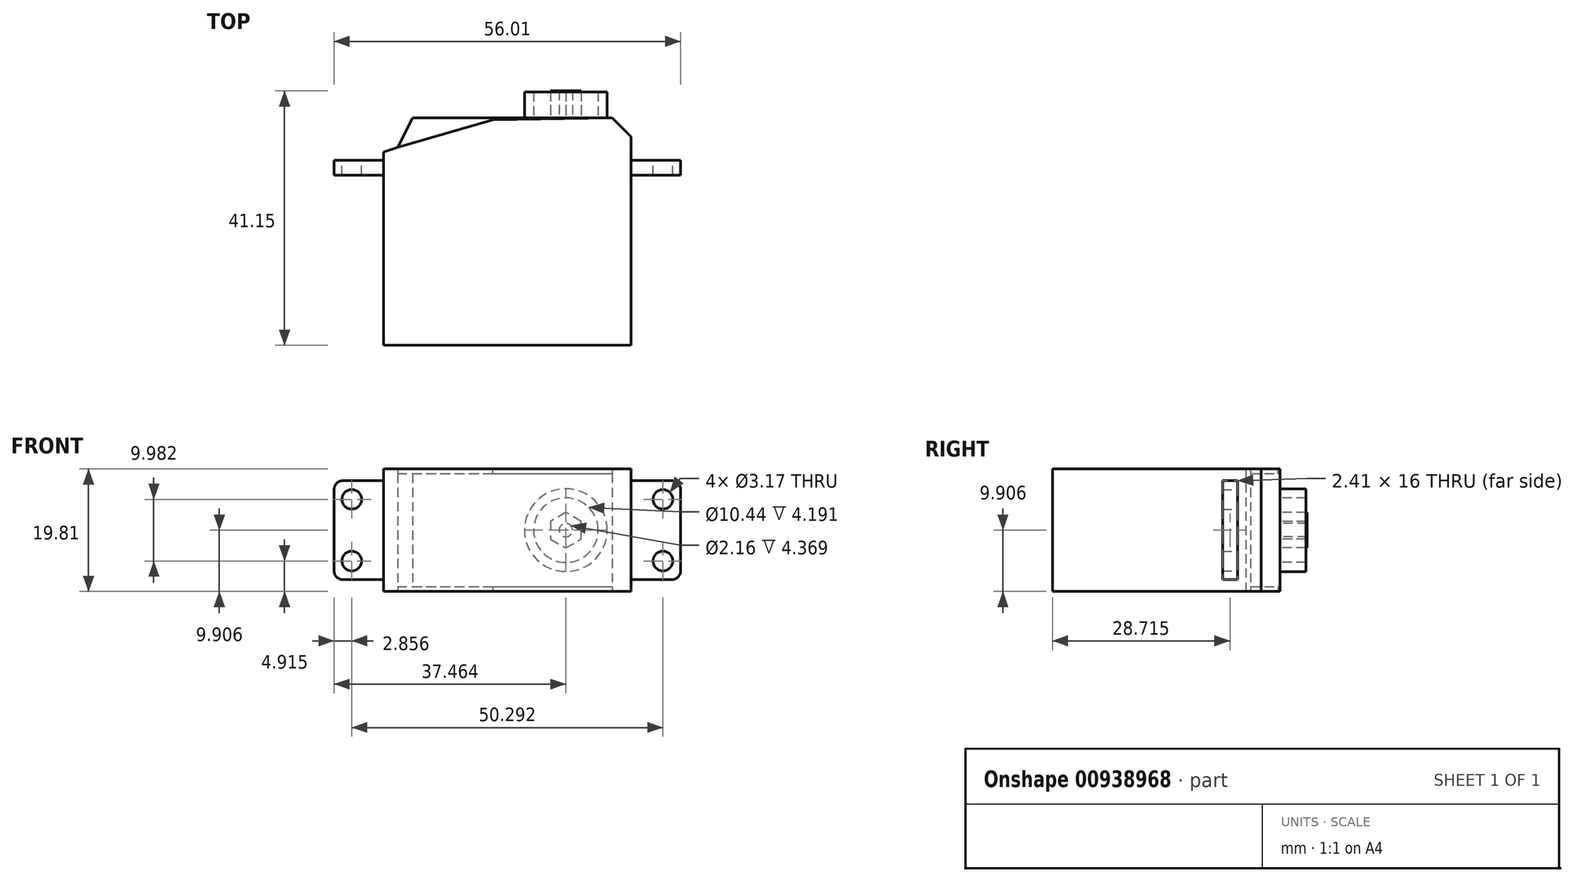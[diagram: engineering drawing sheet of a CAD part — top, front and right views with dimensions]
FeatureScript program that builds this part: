
annotation { "Feature Type Name" : "Feature", "Feature Type Description" : "" }
export const myFeature = defineFeature(function(context is Context, id is Id, definition is map)
    precondition{}
    {
        {
            var Q0;
            Q0=qCreatedBy(makeId("Top.planeOp"),FACE);
            var sketch = newSketch(context, id + "F0", { "sketchPlane" : qUnion([Q0])});
            skLineSegment(sketch, "E0.bottom", {"start": v(0, 0) * mm, "end": v(40, 0) * mm});
            skLineSegment(sketch, "E0.top", {"start": v(0, -36.78) * mm, "end": v(40, -36.78) * mm});
            skLineSegment(sketch, "E0.left", {"start": v(0, 0) * mm, "end": v(0, -36.78) * mm});
            skLineSegment(sketch, "E0.right", {"start": v(40, 0) * mm, "end": v(40, -36.78) * mm});
            skLineSegment(sketch, "E1", {"start": v(0, -5.54) * mm, "end": v(15.88, 0) * mm});
            skLineSegment(sketch, "E2", {"start": v(2.27, -4.75) * mm, "end": v(4.7, 0) * mm});
            skSolve(sketch);
        }
        {
            var Q0;
            {var subQ3=sQuery(id+"F0.wireOp",EDGE,"E0.top");Q0=makeQuery(id+"F0.imprint","IMPRINT",FACE,{"disambiguationData":[TD([[makeQuery(id+"F0.imprint","IMPRINT",EDGE,{"derivedFrom":subQ3}),1.0]])]});}
            extrude(context, id + "F1", {"entities" : qUnion([Q0]), "depth" : 19.8 * mm});
        }
        {
            var Q0;
            Q0=makeQuery(id+"F1.opExtrude","SWEPT_EDGE",EDGE,{"disambiguationData":[OSD([sQuery(id+"F0.wireOp",EDGE,"E0.bottom"),sQuery(id+"F0.wireOp",EDGE,"E0.right")])]});
            chamfer(context, id + "F2", {"entities" : qUnion([Q0]), "width" : 3.05 * mm, "tangentPropagation" : true});
        }
        {
            var Q0;
            {var subQ0=sQuery(id+"F0.wireOp",EDGE,"E2");Q0=makeQuery(id+"F0.imprint","IMPRINT",FACE,{"disambiguationData":[TD([[makeQuery(id+"F0.imprint","IMPRINT",EDGE,{"derivedFrom":subQ0}),-1.0]])]});}
            extrude(context, id + "F3", {"entities" : qUnion([Q0]), "operationType" : NewBodyOperationType.ADD, "depth" : 19.8 * mm});
        }
        {
            var Q0;
            Q0=makeQuery(id+"F1.opExtrude","SWEPT_FACE",FACE,{"disambiguationData":[OSD([sQuery(id+"F0.wireOp",EDGE,"E0.right")])]});
            var sketch = newSketch(context, id + "F4", { "sketchPlane" : qUnion([Q0])});
            skLineSegment(sketch, "E3.bottom", {"start": v(-6.86, 17.9) * mm, "end": v(-9.27, 17.9) * mm});
            skLineSegment(sketch, "E3.top", {"start": v(-6.86, 1.9) * mm, "end": v(-9.27, 1.9) * mm});
            skLineSegment(sketch, "E3.left", {"start": v(-6.86, 17.9) * mm, "end": v(-6.86, 1.9) * mm});
            skLineSegment(sketch, "E3.right", {"start": v(-9.27, 17.9) * mm, "end": v(-9.27, 1.9) * mm});
            skLineSegment(sketch, "E4", {"start": v(-6.86, 9.9) * mm, "end": v(-9.27, 9.9) * mm, "construction": true});
            skLineSegment(sketch, "E5", {"start": v(-6.86, 0) * mm, "end": v(-6.86, 19.81) * mm, "construction": true});
            skSolve(sketch);
        }
        {
            var Q0;
            Q0=qSketchRegion(id+"F4",true);
            extrude(context, id + "F5", {"entities" : qUnion([Q0]), "operationType" : NewBodyOperationType.ADD, "depth" : 8 * mm});
        }
        {
            var Q0;
            Q0=makeQuery(id+"F1.opExtrude","SWEPT_FACE",FACE,{"disambiguationData":[OSD([sQuery(id+"F0.wireOp",EDGE,"E0.left")])]});
            var sketch = newSketch(context, id + "F6", { "sketchPlane" : qUnion([Q0])});
            skLineSegment(sketch, "E6.bottom", {"start": v(6.86, 1.9) * mm, "end": v(9.27, 1.9) * mm});
            skLineSegment(sketch, "E6.top", {"start": v(6.86, 17.9) * mm, "end": v(9.27, 17.9) * mm});
            skLineSegment(sketch, "E6.left", {"start": v(6.86, 1.9) * mm, "end": v(6.86, 17.9) * mm});
            skLineSegment(sketch, "E6.right", {"start": v(9.27, 1.9) * mm, "end": v(9.27, 17.9) * mm});
            skLineSegment(sketch, "E7", {"start": v(9.27, 19.81) * mm, "end": v(9.27, 0) * mm, "construction": true});
            skPoint(sketch, "E8", {"position": v(9.27, 9.9) * mm});
            skSolve(sketch);
        }
        {
            var Q0;
            Q0=qSketchRegion(id+"F6",true);
            extrude(context, id + "F7", {"entities" : qUnion([Q0]), "operationType" : NewBodyOperationType.ADD, "depth" : 8 * mm});
        }
        {
            var Q0;
            Q0=makeQuery(id+"F5.opExtrude","SWEPT_FACE",FACE,{"disambiguationData":[OSD([sQuery(id+"F4.wireOp",EDGE,"E3.left")])]});
            var sketch = newSketch(context, id + "F8", { "sketchPlane" : qUnion([Q0])});
            skCircle(sketch, "E9", {"center": v(-45.15, 14.9) * mm, "radius": 1.59 * mm});
            skCircle(sketch, "E10", {"center": v(-45.15, 4.91) * mm, "radius": 1.59 * mm});
            skCircle(sketch, "E11", {"center": v(5.14, 14.9) * mm, "radius": 1.59 * mm});
            skCircle(sketch, "E12", {"center": v(5.14, 4.91) * mm, "radius": 1.59 * mm});
            skSolve(sketch);
        }
        {
            var Q0;
            Q0=qSketchRegion(id+"F8",true);
            extrude(context, id + "F9", {"entities" : qUnion([Q0]), "operationType" : NewBodyOperationType.REMOVE, "oppositeDirection" : true, "depth" : 25.4 * mm});
        }
        {
            var Q0;
            Q0=qSketchRegion(id+"F8",true);
            extrude(context, id + "F10", {"entities" : qUnion([Q0]), "operationType" : NewBodyOperationType.REMOVE, "oppositeDirection" : true, "depth" : 25.4 * mm});
        }
        {
            var Q0;
            Q0=makeQuery(id+"F5.opExtrude","CAP_EDGE",EDGE,{"disambiguationData":[OSD([sQuery(id+"F4.wireOp",EDGE,"E3.bottom")])],"isStart":false});
            var Q1;
            Q1=makeQuery(id+"F5.opExtrude","CAP_EDGE",EDGE,{"disambiguationData":[OSD([sQuery(id+"F4.wireOp",EDGE,"E3.top")])],"isStart":false});
            var Q2;
            Q2=makeQuery(id+"F7.opExtrude","CAP_EDGE",EDGE,{"disambiguationData":[OSD([sQuery(id+"F6.wireOp",EDGE,"E6.bottom")])],"isStart":false});
            var Q3;
            Q3=makeQuery(id+"F7.opExtrude","CAP_EDGE",EDGE,{"disambiguationData":[OSD([sQuery(id+"F6.wireOp",EDGE,"E6.top")])],"isStart":false});
            fillet(context, id + "F11", {"entities" : qUnion([Q0, Q1, Q2, Q3]), "radius" : 1.4 * mm, "tangentPropagation" : true, "allowEdgeOverflow" : false});
        }
        {
            var Q0;
            {var subQ0=sQuery(id+"F0.wireOp",EDGE,"E0.bottom");var subQ1=sQuery(id+"F0.wireOp",EDGE,"E1");Q0=makeQuery(id+"F3.boolean.opBoolean","MERGE",FACE,{"derivedFrom":[makeQuery(id+"F1.opExtrude","CAP_FACE",FACE,{"disambiguationData":[OSD([subQ0,sQuery(id+"F0.wireOp",EDGE,"E0.top"),sQuery(id+"F0.wireOp",EDGE,"E0.left"),sQuery(id+"F0.wireOp",EDGE,"E0.right"),subQ1])],"isStart":false}),makeQuery(id+"F3.opExtrude","CAP_FACE",FACE,{"disambiguationData":[OSD([subQ0,subQ1,sQuery(id+"F0.wireOp",EDGE,"E2")])],"isStart":false})]});}
            var sketch = newSketch(context, id + "F12", { "sketchPlane" : qUnion([Q0])});
            skLineSegment(sketch, "E13", {"start": v(2.27, -4.75) * mm, "end": v(40, -4.75) * mm});
            skLineSegment(sketch, "E14", {"start": v(2.27, -4.75) * mm, "end": v(17.64, -0.3) * mm});
            skLineSegment(sketch, "E15", {"start": v(17.64, -0.3) * mm, "end": v(36.96, 0) * mm});
            skSolve(sketch);
        }
        {
            var Q0;
            Q0=makeQuery(id+"F12.imprint","IMPRINT",FACE,{"disambiguationData":[TD([[makeQuery(id+"F12.imprint","IMPRINT",EDGE,{"derivedFrom":sQuery(id+"F12.wireOp",EDGE,"E14")}),1.0]])]});
            extrude(context, id + "F13", {"entities" : qUnion([Q0]), "operationType" : NewBodyOperationType.REMOVE, "oppositeDirection" : true, "depth" : 0.76 * mm});
        }
        {
            var Q0;
            {var subQ0=sQuery(id+"F0.wireOp",EDGE,"E0.bottom");var subQ1=sQuery(id+"F0.wireOp",EDGE,"E1");Q0=makeQuery(id+"F3.boolean.opBoolean","MERGE",FACE,{"derivedFrom":[makeQuery(id+"F1.opExtrude","CAP_FACE",FACE,{"disambiguationData":[OSD([subQ0,sQuery(id+"F0.wireOp",EDGE,"E0.top"),sQuery(id+"F0.wireOp",EDGE,"E0.left"),sQuery(id+"F0.wireOp",EDGE,"E0.right"),subQ1])],"isStart":true}),makeQuery(id+"F3.opExtrude","CAP_FACE",FACE,{"disambiguationData":[OSD([subQ0,subQ1,sQuery(id+"F0.wireOp",EDGE,"E2")])],"isStart":true})]});}
            var sketch = newSketch(context, id + "F14", { "sketchPlane" : qUnion([Q0])});
            skLineSegment(sketch, "E16", {"start": v(2.27, 4.75) * mm, "end": v(40, 4.75) * mm});
            skLineSegment(sketch, "E17", {"start": v(2.27, 4.75) * mm, "end": v(17.64, 0.3) * mm});
            skLineSegment(sketch, "E18", {"start": v(17.64, 0.3) * mm, "end": v(36.96, 0) * mm});
            skSolve(sketch);
        }
        {
            var Q0;
            Q0=makeQuery(id+"F14.imprint","IMPRINT",FACE,{"disambiguationData":[TD([[makeQuery(id+"F14.imprint","IMPRINT",EDGE,{"derivedFrom":sQuery(id+"F14.wireOp",EDGE,"E17")}),-1.0]])]});
            extrude(context, id + "F15", {"entities" : qUnion([Q0]), "operationType" : NewBodyOperationType.REMOVE, "oppositeDirection" : true, "depth" : 0.76 * mm});
        }
        {
            var Q0;
            {var subQ0=sQuery(id+"F0.wireOp",EDGE,"E0.bottom");Q0=makeQuery(id+"F3.boolean.opBoolean","MERGE",FACE,{"derivedFrom":[makeQuery(id+"F1.opExtrude","SWEPT_FACE",FACE,{"disambiguationData":[OSD([subQ0])]}),makeQuery(id+"F3.opExtrude","SWEPT_FACE",FACE,{"disambiguationData":[OSD([subQ0])]})]});}
            var sketch = newSketch(context, id + "F16", { "sketchPlane" : qUnion([Q0])});
            skCircle(sketch, "E19", {"center": v(-29.46, 9.9) * mm, "radius": 9.14 * mm});
            skCircle(sketch, "E20", {"center": v(-29.46, 9.9) * mm, "radius": 6.7 * mm});
            skCircle(sketch, "E21", {"center": v(-29.46, 9.9) * mm, "radius": 5.22 * mm});
            skPoint(sketch, "E22.orphan", {"position": v(-29.46, 19.05) * mm});
            skPoint(sketch, "E23.orphan", {"position": v(-29.46, 0.76) * mm});
            skCircle(sketch, "E24.cCircle", {"center": v(-29.46, 9.9) * mm, "radius": 2.49 * mm, "construction": true});
            skLineSegment(sketch, "E24.0", {"start": v(-31.95, 8.47) * mm, "end": v(-31.95, 11.34) * mm});
            skLineSegment(sketch, "E24.1", {"start": v(-31.95, 11.34) * mm, "end": v(-29.46, 12.78) * mm});
            skLineSegment(sketch, "E24.2", {"start": v(-29.46, 12.78) * mm, "end": v(-26.97, 11.34) * mm});
            skLineSegment(sketch, "E24.3", {"start": v(-26.97, 11.34) * mm, "end": v(-26.97, 8.47) * mm});
            skLineSegment(sketch, "E24.4", {"start": v(-26.97, 8.47) * mm, "end": v(-29.46, 7.03) * mm});
            skLineSegment(sketch, "E24.5", {"start": v(-29.46, 7.03) * mm, "end": v(-31.95, 8.47) * mm});
            skPoint(sketch, "E24.0.midPoint", {"position": v(-31.95, 9.9) * mm});
            skCircle(sketch, "E25", {"center": v(-29.46, 9.9) * mm, "radius": 1.08 * mm});
            skSolve(sketch);
        }
        {
            var Q0;
            Q0=makeQuery(id+"F16.imprint","IMPRINT",FACE,{"disambiguationData":[TD([[makeQuery(id+"F16.imprint","IMPRINT",EDGE,{"derivedFrom":sQuery(id+"F16.wireOp",EDGE,"E20")}),1.0]])]});
            extrude(context, id + "F17", {"entities" : qUnion([Q0]), "operationType" : NewBodyOperationType.ADD, "depth" : 4.2 * mm});
        }
        {
            var Q0;
            Q0=makeQuery(id+"F16.imprint","IMPRINT",FACE,{"disambiguationData":[TD([[makeQuery(id+"F16.imprint","IMPRINT",EDGE,{"derivedFrom":sQuery(id+"F16.wireOp",EDGE,"E24.0")}),-1.0]])]});
            extrude(context, id + "F18", {"entities" : qUnion([Q0]), "operationType" : NewBodyOperationType.ADD, "depth" : 4.37 * mm});
        }
    });
